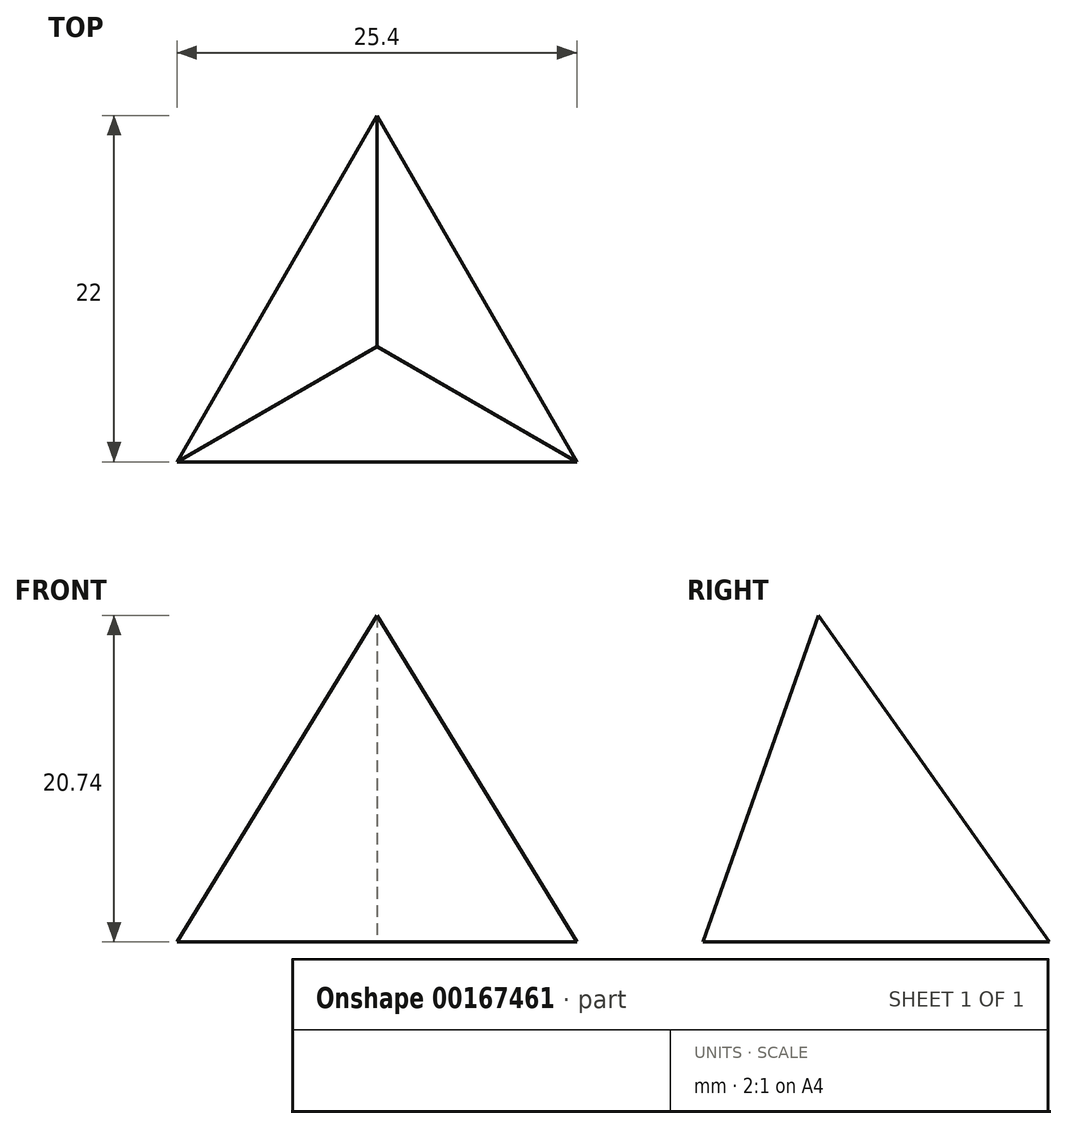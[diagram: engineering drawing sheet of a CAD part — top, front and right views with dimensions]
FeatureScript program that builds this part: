
annotation { "Feature Type Name" : "Feature", "Feature Type Description" : "" }
export const myFeature = defineFeature(function(context is Context, id is Id, definition is map)
    precondition{}
    {
        {
            var Q0;
            Q0=qCreatedBy(makeId("Top.planeOp"),FACE);
            var sketch = newSketch(context, id + "F0", { "sketchPlane" : qUnion([Q0])});
            skLineSegment(sketch, "E0", {"start": v(-12.7, 0) * mm, "end": v(12.7, 0) * mm});
            skLineSegment(sketch, "E1", {"start": v(12.7, 0) * mm, "end": v(0, 22) * mm});
            skLineSegment(sketch, "E2", {"start": v(0, 22) * mm, "end": v(-12.7, 0) * mm});
            skSolve(sketch);
        }
        {
            var Q0;
            Q0=makeQuery(id+"F0.imprint","IMPRINT",FACE,{"disambiguationData":[TD([[makeQuery(id+"F0.imprint","IMPRINT",EDGE,{"derivedFrom":sQuery(id+"F0.wireOp",EDGE,"E0")}),1.0]])]});
            extrude(context, id + "F1", {"entities" : qUnion([Q0]), "depth" : 25.4 * mm, "hasDraft" : true, "draftAngle" : 90 * degree - atan(2 * (2 ^ 0.5)), "draftPullDirection" : true});
        }
    });
